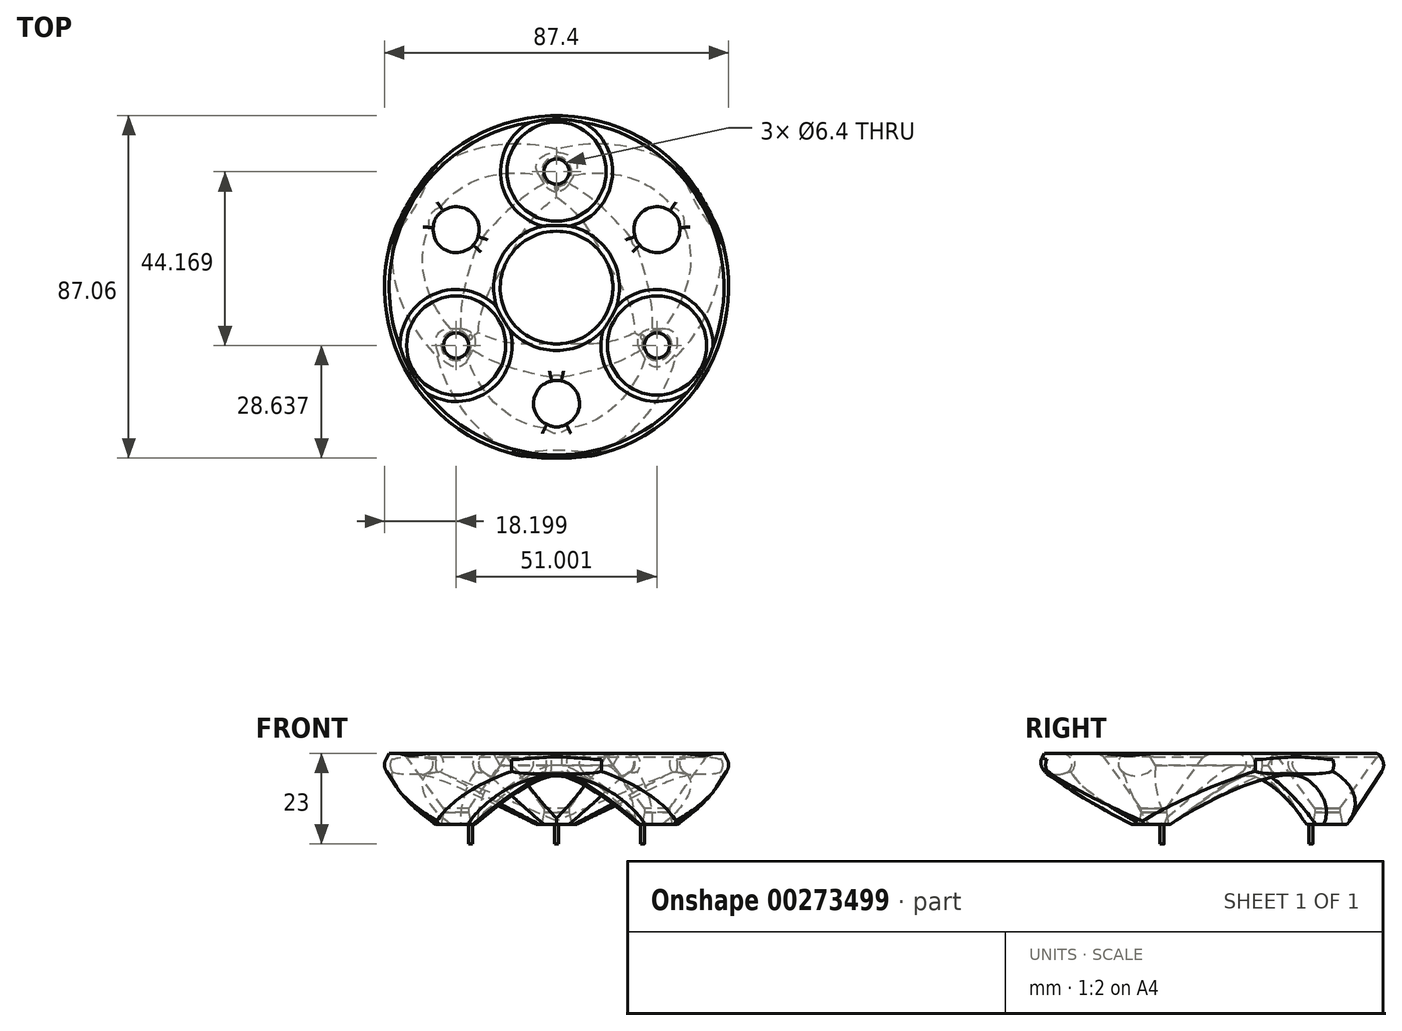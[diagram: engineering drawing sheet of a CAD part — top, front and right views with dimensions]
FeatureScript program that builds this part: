
annotation { "Feature Type Name" : "Feature", "Feature Type Description" : "" }
export const myFeature = defineFeature(function(context is Context, id is Id, definition is map)
    precondition{}
    {
        {
            var Q0;
            Q0=qCreatedBy(makeId("Top.planeOp"),FACE);
            var sketch = newSketch(context, id + "F0", { "sketchPlane" : qUnion([Q0])});
            skCircle(sketch, "E0", {"center": v(0, 0) * mm, "radius": 47.5 * mm});
            skCircle(sketch, "E1", {"center": v(0, 0) * mm, "radius": 11 * mm});
            skCircle(sketch, "E2", {"center": v(0, 29.45) * mm, "radius": 3.2 * mm});
            skCircle(sketch, "E3.1.0", {"center": v(-25.5, 14.72) * mm, "radius": 3.2 * mm});
            skCircle(sketch, "E3.2.0", {"center": v(-25.5, -14.72) * mm, "radius": 3.2 * mm});
            skCircle(sketch, "E4.1.3.0", {"center": v(0, -29.45) * mm, "radius": 3.2 * mm});
            skCircle(sketch, "E4.1.4.0", {"center": v(25.5, -14.72) * mm, "radius": 3.2 * mm});
            skCircle(sketch, "E4.1.5.0", {"center": v(25.5, 14.72) * mm, "radius": 3.2 * mm});
            skCircle(sketch, "E5", {"center": v(0, 25.2) * mm, "radius": 0.5 * mm});
            skCircle(sketch, "E6.1.0", {"center": v(-21.83, -12.6) * mm, "radius": 0.5 * mm});
            skCircle(sketch, "E6.2.0", {"center": v(21.83, -12.6) * mm, "radius": 0.5 * mm});
            skSolve(sketch);
        }
        {
            var Q0;
            Q0=makeQuery(id+"F0.imprint","IMPRINT",FACE,{"disambiguationData":[TD([[makeQuery(id+"F0.imprint","IMPRINT",EDGE,{"derivedFrom":sQuery(id+"F0.wireOp",EDGE,"E0")}),1.0]])]});
            var Q1;
            Q1=makeQuery(id+"F0.imprint","IMPRINT",FACE,{"disambiguationData":[TD([[makeQuery(id+"F0.imprint","IMPRINT",EDGE,{"derivedFrom":sQuery(id+"F0.wireOp",EDGE,"E6.1.0")}),1.0]])]});
            var Q2;
            Q2=makeQuery(id+"F0.imprint","IMPRINT",FACE,{"disambiguationData":[TD([[makeQuery(id+"F0.imprint","IMPRINT",EDGE,{"derivedFrom":sQuery(id+"F0.wireOp",EDGE,"E6.2.0")}),1.0]])]});
            var Q3;
            Q3=makeQuery(id+"F0.imprint","IMPRINT",FACE,{"disambiguationData":[TD([[makeQuery(id+"F0.imprint","IMPRINT",EDGE,{"derivedFrom":sQuery(id+"F0.wireOp",EDGE,"E5")}),1.0]])]});
            extrude(context, id + "F1", {"entities" : qUnion([Q0, Q1, Q2, Q3]), "depth" : 18 * mm, "offsetDistance" : 25 * mm});
        }
        {
            var Q0;
            Q0=makeQuery(id+"F0.imprint","IMPRINT",FACE,{"disambiguationData":[TD([[makeQuery(id+"F0.imprint","IMPRINT",EDGE,{"derivedFrom":sQuery(id+"F0.wireOp",EDGE,"E5")}),1.0]])]});
            var Q1;
            Q1=makeQuery(id+"F0.imprint","IMPRINT",FACE,{"disambiguationData":[TD([[makeQuery(id+"F0.imprint","IMPRINT",EDGE,{"derivedFrom":sQuery(id+"F0.wireOp",EDGE,"E6.1.0")}),1.0]])]});
            var Q2;
            Q2=makeQuery(id+"F0.imprint","IMPRINT",FACE,{"disambiguationData":[TD([[makeQuery(id+"F0.imprint","IMPRINT",EDGE,{"derivedFrom":sQuery(id+"F0.wireOp",EDGE,"E6.2.0")}),1.0]])]});
            extrude(context, id + "F2", {"entities" : qUnion([Q0, Q1, Q2]), "operationType" : NewBodyOperationType.ADD, "depth" : 10 * mm, "symmetric" : true});
        }
        {
            var Q0;
            Q0=makeQuery(id+"F1.opExtrude","CAP_EDGE",EDGE,{"disambiguationData":[OSD([sQuery(id+"F0.wireOp",EDGE,"E2")])],"isStart":false});
            var Q1;
            Q1=makeQuery(id+"F1.opExtrude","CAP_EDGE",EDGE,{"disambiguationData":[OSD([sQuery(id+"F0.wireOp",EDGE,"E4.1.4.0")])],"isStart":false});
            var Q2;
            Q2=makeQuery(id+"F1.opExtrude","CAP_EDGE",EDGE,{"disambiguationData":[OSD([sQuery(id+"F0.wireOp",EDGE,"E3.2.0")])],"isStart":false});
            chamfer(context, id + "F3", {"entities" : qUnion([Q0, Q1, Q2]), "chamferType" : ChamferType.TWO_OFFSETS, "width1" : 14 * mm, "oppositeDirection" : false, "width2" : 10 * mm, "tangentPropagation" : true});
        }
        {
            var Q0;
            Q0=makeQuery(id+"F1.opExtrude","CAP_EDGE",EDGE,{"disambiguationData":[OSD([sQuery(id+"F0.wireOp",EDGE,"E0")])],"isStart":true});
            chamfer(context, id + "F4", {"entities" : qUnion([Q0]), "chamferType" : ChamferType.TWO_OFFSETS, "width1" : 20 * mm, "oppositeDirection" : false, "width2" : 13 * mm, "tangentPropagation" : true});
        }
        {
            var Q0;
            Q0=makeQuery(id+"F1.opExtrude","CAP_EDGE",EDGE,{"disambiguationData":[OSD([sQuery(id+"F0.wireOp",EDGE,"E2")])],"isStart":true});
            var Q1;
            Q1=makeQuery(id+"F1.opExtrude","CAP_EDGE",EDGE,{"disambiguationData":[OSD([sQuery(id+"F0.wireOp",EDGE,"E3.2.0")])],"isStart":true});
            var Q2;
            Q2=makeQuery(id+"F1.opExtrude","CAP_EDGE",EDGE,{"disambiguationData":[OSD([sQuery(id+"F0.wireOp",EDGE,"E4.1.4.0")])],"isStart":true});
            chamfer(context, id + "F5", {"entities" : qUnion([Q0, Q1, Q2]), "chamferType" : ChamferType.TWO_OFFSETS, "width1" : 0.6 * mm, "oppositeDirection" : false, "width2" : 3 * mm, "tangentPropagation" : true});
        }
        {
            var Q0;
            Q0=makeQuery(id+"F1.opExtrude","CAP_EDGE",EDGE,{"disambiguationData":[OSD([sQuery(id+"F0.wireOp",EDGE,"E1")])],"isStart":true});
            chamfer(context, id + "F6", {"entities" : qUnion([Q0]), "chamferType" : ChamferType.TWO_OFFSETS, "width1" : 13 * mm, "oppositeDirection" : false, "width2" : 20 * mm, "tangentPropagation" : true});
        }
        {
            var Q0;
            Q0=makeQuery(id+"F1.opExtrude","CAP_EDGE",EDGE,{"disambiguationData":[OSD([sQuery(id+"F0.wireOp",EDGE,"E4.1.5.0")])],"isStart":true});
            var Q1;
            Q1=makeQuery(id+"F1.opExtrude","CAP_EDGE",EDGE,{"disambiguationData":[OSD([sQuery(id+"F0.wireOp",EDGE,"E4.1.3.0")])],"isStart":true});
            var Q2;
            Q2=makeQuery(id+"F1.opExtrude","CAP_EDGE",EDGE,{"disambiguationData":[OSD([sQuery(id+"F0.wireOp",EDGE,"E3.1.0")])],"isStart":true});
            chamfer(context, id + "F7", {"entities" : qUnion([Q0, Q1, Q2]), "chamferType" : ChamferType.TWO_OFFSETS, "width1" : 22 * mm, "oppositeDirection" : false, "width2" : 16 * mm, "tangentPropagation" : true});
        }
        {
            var Q0;
            {var subQ0=sQuery(id+"F0.wireOp",EDGE,"E0");Q0=makeQuery(id+"F4.opChamfer","BLEND_EDGE",EDGE,{"blendedFrom":[makeQuery(id+"F1.opExtrude","CAP_EDGE",EDGE,{"disambiguationData":[OSD([subQ0])],"isStart":true}),makeQuery(id+"F1.opExtrude","CAP_FACE",FACE,{"disambiguationData":[OSD([subQ0,sQuery(id+"F0.wireOp",EDGE,"E1"),sQuery(id+"F0.wireOp",EDGE,"E2"),sQuery(id+"F0.wireOp",EDGE,"E3.1.0"),sQuery(id+"F0.wireOp",EDGE,"E3.2.0")])],"isStart":false})],"blendedInto":[makeQuery(id+"F1.opExtrude","CAP_FACE",FACE,{"disambiguationData":[OSD([subQ0,sQuery(id+"F0.wireOp",EDGE,"E1"),sQuery(id+"F0.wireOp",EDGE,"E2"),sQuery(id+"F0.wireOp",EDGE,"E3.1.0"),sQuery(id+"F0.wireOp",EDGE,"E3.2.0")])],"isStart":false})]});}
            var Q1;
            {var subQ0=sQuery(id+"F0.wireOp",EDGE,"E1");Q1=makeQuery(id+"F6.opChamfer","BLEND_EDGE",EDGE,{"blendedFrom":[makeQuery(id+"F1.opExtrude","CAP_EDGE",EDGE,{"disambiguationData":[OSD([subQ0])],"isStart":true}),makeQuery(id+"F1.opExtrude","CAP_FACE",FACE,{"disambiguationData":[OSD([sQuery(id+"F0.wireOp",EDGE,"E0"),subQ0,sQuery(id+"F0.wireOp",EDGE,"E2"),sQuery(id+"F0.wireOp",EDGE,"E3.1.0"),sQuery(id+"F0.wireOp",EDGE,"E3.2.0")])],"isStart":false})],"blendedInto":[makeQuery(id+"F1.opExtrude","CAP_FACE",FACE,{"disambiguationData":[OSD([sQuery(id+"F0.wireOp",EDGE,"E0"),subQ0,sQuery(id+"F0.wireOp",EDGE,"E2"),sQuery(id+"F0.wireOp",EDGE,"E3.1.0"),sQuery(id+"F0.wireOp",EDGE,"E3.2.0")])],"isStart":false})]});}
            var Q2;
            {var subQ0=sQuery(id+"F0.wireOp",EDGE,"E3.2.0");Q2=makeQuery(id+"F3.opChamfer","BLEND_EDGE",EDGE,{"blendedFrom":[makeQuery(id+"F1.opExtrude","CAP_EDGE",EDGE,{"disambiguationData":[OSD([subQ0])],"isStart":false}),makeQuery(id+"F1.opExtrude","CAP_FACE",FACE,{"disambiguationData":[OSD([sQuery(id+"F0.wireOp",EDGE,"E0"),sQuery(id+"F0.wireOp",EDGE,"E1"),sQuery(id+"F0.wireOp",EDGE,"E2"),sQuery(id+"F0.wireOp",EDGE,"E3.1.0"),subQ0,sQuery(id+"F0.wireOp",EDGE,"E4.1.3.0"),sQuery(id+"F0.wireOp",EDGE,"E4.1.4.0"),sQuery(id+"F0.wireOp",EDGE,"E4.1.5.0")])],"isStart":false})],"blendedInto":[makeQuery(id+"F1.opExtrude","CAP_FACE",FACE,{"disambiguationData":[OSD([sQuery(id+"F0.wireOp",EDGE,"E0"),sQuery(id+"F0.wireOp",EDGE,"E1"),sQuery(id+"F0.wireOp",EDGE,"E2"),sQuery(id+"F0.wireOp",EDGE,"E3.1.0"),subQ0,sQuery(id+"F0.wireOp",EDGE,"E4.1.3.0"),sQuery(id+"F0.wireOp",EDGE,"E4.1.4.0"),sQuery(id+"F0.wireOp",EDGE,"E4.1.5.0")])],"isStart":false})]});}
            var Q3;
            {var subQ0=sQuery(id+"F0.wireOp",EDGE,"E2");Q3=makeQuery(id+"F3.opChamfer","BLEND_EDGE",EDGE,{"blendedFrom":[makeQuery(id+"F1.opExtrude","CAP_EDGE",EDGE,{"disambiguationData":[OSD([subQ0])],"isStart":false}),makeQuery(id+"F1.opExtrude","CAP_FACE",FACE,{"disambiguationData":[OSD([sQuery(id+"F0.wireOp",EDGE,"E0"),sQuery(id+"F0.wireOp",EDGE,"E1"),subQ0,sQuery(id+"F0.wireOp",EDGE,"E3.1.0"),sQuery(id+"F0.wireOp",EDGE,"E3.2.0"),sQuery(id+"F0.wireOp",EDGE,"E4.1.3.0"),sQuery(id+"F0.wireOp",EDGE,"E4.1.4.0"),sQuery(id+"F0.wireOp",EDGE,"E4.1.5.0")])],"isStart":false})],"blendedInto":[makeQuery(id+"F1.opExtrude","CAP_FACE",FACE,{"disambiguationData":[OSD([sQuery(id+"F0.wireOp",EDGE,"E0"),sQuery(id+"F0.wireOp",EDGE,"E1"),subQ0,sQuery(id+"F0.wireOp",EDGE,"E3.1.0"),sQuery(id+"F0.wireOp",EDGE,"E3.2.0"),sQuery(id+"F0.wireOp",EDGE,"E4.1.3.0"),sQuery(id+"F0.wireOp",EDGE,"E4.1.4.0"),sQuery(id+"F0.wireOp",EDGE,"E4.1.5.0")])],"isStart":false})]});}
            var Q4;
            {var subQ0=sQuery(id+"F0.wireOp",EDGE,"E4.1.4.0");Q4=makeQuery(id+"F3.opChamfer","BLEND_EDGE",EDGE,{"blendedFrom":[makeQuery(id+"F1.opExtrude","CAP_EDGE",EDGE,{"disambiguationData":[OSD([subQ0])],"isStart":false}),makeQuery(id+"F1.opExtrude","CAP_FACE",FACE,{"disambiguationData":[OSD([sQuery(id+"F0.wireOp",EDGE,"E0"),sQuery(id+"F0.wireOp",EDGE,"E1"),sQuery(id+"F0.wireOp",EDGE,"E2"),sQuery(id+"F0.wireOp",EDGE,"E3.1.0"),sQuery(id+"F0.wireOp",EDGE,"E3.2.0"),sQuery(id+"F0.wireOp",EDGE,"E4.1.3.0"),subQ0,sQuery(id+"F0.wireOp",EDGE,"E4.1.5.0")])],"isStart":false})],"blendedInto":[makeQuery(id+"F1.opExtrude","CAP_FACE",FACE,{"disambiguationData":[OSD([sQuery(id+"F0.wireOp",EDGE,"E0"),sQuery(id+"F0.wireOp",EDGE,"E1"),sQuery(id+"F0.wireOp",EDGE,"E2"),sQuery(id+"F0.wireOp",EDGE,"E3.1.0"),sQuery(id+"F0.wireOp",EDGE,"E3.2.0"),sQuery(id+"F0.wireOp",EDGE,"E4.1.3.0"),subQ0,sQuery(id+"F0.wireOp",EDGE,"E4.1.5.0")])],"isStart":false})]});}
            var Q5;
            {var subQ0=sQuery(id+"F0.wireOp",EDGE,"E3.1.0");Q5=makeQuery(id+"F7.opChamfer","BLEND_EDGE",EDGE,{"blendedFrom":[makeQuery(id+"F1.opExtrude","CAP_EDGE",EDGE,{"disambiguationData":[OSD([subQ0])],"isStart":true}),makeQuery(id+"F1.opExtrude","CAP_FACE",FACE,{"disambiguationData":[OSD([sQuery(id+"F0.wireOp",EDGE,"E0"),sQuery(id+"F0.wireOp",EDGE,"E1"),sQuery(id+"F0.wireOp",EDGE,"E2"),subQ0,sQuery(id+"F0.wireOp",EDGE,"E3.2.0"),sQuery(id+"F0.wireOp",EDGE,"E4.1.3.0"),sQuery(id+"F0.wireOp",EDGE,"E4.1.4.0"),sQuery(id+"F0.wireOp",EDGE,"E4.1.5.0")])],"isStart":false})],"blendedInto":[makeQuery(id+"F1.opExtrude","CAP_FACE",FACE,{"disambiguationData":[OSD([sQuery(id+"F0.wireOp",EDGE,"E0"),sQuery(id+"F0.wireOp",EDGE,"E1"),sQuery(id+"F0.wireOp",EDGE,"E2"),subQ0,sQuery(id+"F0.wireOp",EDGE,"E3.2.0"),sQuery(id+"F0.wireOp",EDGE,"E4.1.3.0"),sQuery(id+"F0.wireOp",EDGE,"E4.1.4.0"),sQuery(id+"F0.wireOp",EDGE,"E4.1.5.0")])],"isStart":false})]});}
            var Q6;
            {var subQ0=sQuery(id+"F0.wireOp",EDGE,"E4.1.3.0");Q6=makeQuery(id+"F7.opChamfer","BLEND_EDGE",EDGE,{"blendedFrom":[makeQuery(id+"F1.opExtrude","CAP_EDGE",EDGE,{"disambiguationData":[OSD([subQ0])],"isStart":true}),makeQuery(id+"F1.opExtrude","CAP_FACE",FACE,{"disambiguationData":[OSD([sQuery(id+"F0.wireOp",EDGE,"E0"),sQuery(id+"F0.wireOp",EDGE,"E1"),sQuery(id+"F0.wireOp",EDGE,"E2"),sQuery(id+"F0.wireOp",EDGE,"E3.1.0"),sQuery(id+"F0.wireOp",EDGE,"E3.2.0"),subQ0,sQuery(id+"F0.wireOp",EDGE,"E4.1.4.0"),sQuery(id+"F0.wireOp",EDGE,"E4.1.5.0")])],"isStart":false})],"blendedInto":[makeQuery(id+"F1.opExtrude","CAP_FACE",FACE,{"disambiguationData":[OSD([sQuery(id+"F0.wireOp",EDGE,"E0"),sQuery(id+"F0.wireOp",EDGE,"E1"),sQuery(id+"F0.wireOp",EDGE,"E2"),sQuery(id+"F0.wireOp",EDGE,"E3.1.0"),sQuery(id+"F0.wireOp",EDGE,"E3.2.0"),subQ0,sQuery(id+"F0.wireOp",EDGE,"E4.1.4.0"),sQuery(id+"F0.wireOp",EDGE,"E4.1.5.0")])],"isStart":false})]});}
            var Q7;
            {var subQ0=sQuery(id+"F0.wireOp",EDGE,"E4.1.5.0");Q7=makeQuery(id+"F7.opChamfer","BLEND_EDGE",EDGE,{"blendedFrom":[makeQuery(id+"F1.opExtrude","CAP_EDGE",EDGE,{"disambiguationData":[OSD([subQ0])],"isStart":true}),makeQuery(id+"F1.opExtrude","CAP_FACE",FACE,{"disambiguationData":[OSD([sQuery(id+"F0.wireOp",EDGE,"E0"),sQuery(id+"F0.wireOp",EDGE,"E1"),sQuery(id+"F0.wireOp",EDGE,"E2"),sQuery(id+"F0.wireOp",EDGE,"E3.1.0"),sQuery(id+"F0.wireOp",EDGE,"E3.2.0"),sQuery(id+"F0.wireOp",EDGE,"E4.1.3.0"),sQuery(id+"F0.wireOp",EDGE,"E4.1.4.0"),subQ0])],"isStart":false})],"blendedInto":[makeQuery(id+"F1.opExtrude","CAP_FACE",FACE,{"disambiguationData":[OSD([sQuery(id+"F0.wireOp",EDGE,"E0"),sQuery(id+"F0.wireOp",EDGE,"E1"),sQuery(id+"F0.wireOp",EDGE,"E2"),sQuery(id+"F0.wireOp",EDGE,"E3.1.0"),sQuery(id+"F0.wireOp",EDGE,"E3.2.0"),sQuery(id+"F0.wireOp",EDGE,"E4.1.3.0"),sQuery(id+"F0.wireOp",EDGE,"E4.1.4.0"),subQ0])],"isStart":false})]});}
            chamfer(context, id + "F8", {"entities" : qUnion([Q0, Q1, Q2, Q3, Q4, Q5, Q6, Q7]), "width" : 2 * mm, "tangentPropagation" : true});
        }
        {
            var Q0;
            Q0=makeQuery(id+"F7.opChamfer","BLEND_EDGE",EDGE,{"blendedFrom":[makeQuery(id+"F1.opExtrude","CAP_EDGE",EDGE,{"disambiguationData":[OSD([sQuery(id+"F0.wireOp",EDGE,"E4.1.5.0")])],"isStart":true}),makeQuery(id+"F6.opChamfer","BLEND_FACE",FACE,{"disambiguationData":[OSD([sQuery(id+"F0.wireOp",EDGE,"E1")])]})],"blendedInto":[makeQuery(id+"F6.opChamfer","BLEND_FACE",FACE,{"disambiguationData":[OSD([sQuery(id+"F0.wireOp",EDGE,"E1")])]})]});
            var Q1;
            Q1=makeQuery(id+"F7.opChamfer","BLEND_EDGE",EDGE,{"blendedFrom":[makeQuery(id+"F1.opExtrude","CAP_EDGE",EDGE,{"disambiguationData":[OSD([sQuery(id+"F0.wireOp",EDGE,"E3.1.0")])],"isStart":true}),makeQuery(id+"F6.opChamfer","BLEND_FACE",FACE,{"disambiguationData":[OSD([sQuery(id+"F0.wireOp",EDGE,"E1")])]})],"blendedInto":[makeQuery(id+"F6.opChamfer","BLEND_FACE",FACE,{"disambiguationData":[OSD([sQuery(id+"F0.wireOp",EDGE,"E1")])]})]});
            var Q2;
            Q2=makeQuery(id+"F7.opChamfer","BLEND_EDGE",EDGE,{"blendedFrom":[makeQuery(id+"F1.opExtrude","CAP_EDGE",EDGE,{"disambiguationData":[OSD([sQuery(id+"F0.wireOp",EDGE,"E4.1.3.0")])],"isStart":true}),makeQuery(id+"F6.opChamfer","BLEND_FACE",FACE,{"disambiguationData":[OSD([sQuery(id+"F0.wireOp",EDGE,"E1")])]})],"blendedInto":[makeQuery(id+"F6.opChamfer","BLEND_FACE",FACE,{"disambiguationData":[OSD([sQuery(id+"F0.wireOp",EDGE,"E1")])]})]});
            var Q3;
            Q3=makeQuery(id+"F7.opChamfer","BLEND_EDGE",EDGE,{"blendedFrom":[makeQuery(id+"F1.opExtrude","CAP_EDGE",EDGE,{"disambiguationData":[OSD([sQuery(id+"F0.wireOp",EDGE,"E3.1.0")])],"isStart":true}),makeQuery(id+"F4.opChamfer","BLEND_FACE",FACE,{"disambiguationData":[OSD([sQuery(id+"F0.wireOp",EDGE,"E0")])]})],"blendedInto":[makeQuery(id+"F4.opChamfer","BLEND_FACE",FACE,{"disambiguationData":[OSD([sQuery(id+"F0.wireOp",EDGE,"E0")])]})]});
            var Q4;
            Q4=makeQuery(id+"F7.opChamfer","BLEND_EDGE",EDGE,{"blendedFrom":[makeQuery(id+"F1.opExtrude","CAP_EDGE",EDGE,{"disambiguationData":[OSD([sQuery(id+"F0.wireOp",EDGE,"E4.1.5.0")])],"isStart":true}),makeQuery(id+"F4.opChamfer","BLEND_FACE",FACE,{"disambiguationData":[OSD([sQuery(id+"F0.wireOp",EDGE,"E0")])]})],"blendedInto":[makeQuery(id+"F4.opChamfer","BLEND_FACE",FACE,{"disambiguationData":[OSD([sQuery(id+"F0.wireOp",EDGE,"E0")])]})]});
            var Q5;
            Q5=makeQuery(id+"F7.opChamfer","BLEND_EDGE",EDGE,{"blendedFrom":[makeQuery(id+"F1.opExtrude","CAP_EDGE",EDGE,{"disambiguationData":[OSD([sQuery(id+"F0.wireOp",EDGE,"E4.1.3.0")])],"isStart":true}),makeQuery(id+"F4.opChamfer","BLEND_FACE",FACE,{"disambiguationData":[OSD([sQuery(id+"F0.wireOp",EDGE,"E0")])]})],"blendedInto":[makeQuery(id+"F4.opChamfer","BLEND_FACE",FACE,{"disambiguationData":[OSD([sQuery(id+"F0.wireOp",EDGE,"E0")])]})]});
            var Q6;
            {var subQ0=sQuery(id+"F0.wireOp",EDGE,"E3.1.0");Q6=makeQuery(id+"F7.opChamfer","BLEND_EDGE",EDGE,{"blendedFrom":[makeQuery(id+"F1.opExtrude","CAP_EDGE",EDGE,{"disambiguationData":[OSD([subQ0])],"isStart":true}),makeQuery(id+"F1.opExtrude","SWEPT_FACE",FACE,{"disambiguationData":[OSD([subQ0])]})],"blendedInto":[makeQuery(id+"F1.opExtrude","SWEPT_FACE",FACE,{"disambiguationData":[OSD([subQ0])]})]});}
            var Q7;
            {var subQ0=sQuery(id+"F0.wireOp",EDGE,"E4.1.5.0");Q7=makeQuery(id+"F7.opChamfer","BLEND_EDGE",EDGE,{"blendedFrom":[makeQuery(id+"F1.opExtrude","CAP_EDGE",EDGE,{"disambiguationData":[OSD([subQ0])],"isStart":true}),makeQuery(id+"F1.opExtrude","SWEPT_FACE",FACE,{"disambiguationData":[OSD([subQ0])]})],"blendedInto":[makeQuery(id+"F1.opExtrude","SWEPT_FACE",FACE,{"disambiguationData":[OSD([subQ0])]})]});}
            var Q8;
            {var subQ0=sQuery(id+"F0.wireOp",EDGE,"E4.1.3.0");Q8=makeQuery(id+"F7.opChamfer","BLEND_EDGE",EDGE,{"blendedFrom":[makeQuery(id+"F1.opExtrude","CAP_EDGE",EDGE,{"disambiguationData":[OSD([subQ0])],"isStart":true}),makeQuery(id+"F1.opExtrude","SWEPT_FACE",FACE,{"disambiguationData":[OSD([subQ0])]})],"blendedInto":[makeQuery(id+"F1.opExtrude","SWEPT_FACE",FACE,{"disambiguationData":[OSD([subQ0])]})]});}
            fillet(context, id + "F9", {"entities" : qUnion([Q0, Q1, Q2, Q3, Q4, Q5, Q6, Q7, Q8]), "radius" : 6 * mm, "tangentPropagation" : true, "allowEdgeOverflow" : false});
        }
        {
            var Q0;
            {var subQ0=sQuery(id+"F0.wireOp",EDGE,"E4.1.5.0");Q0=makeQuery(id+"F3XoC3uYJy4NfSD_1.opFillet","BLEND_EDGE",EDGE,{"blendedFrom":[makeQuery(id+"F1.opExtrude","CAP_EDGE",EDGE,{"disambiguationData":[OSD([subQ0])],"isStart":false}),makeQuery(id+"F9.opFillet","BLEND_FACE",FACE,{"disambiguationData":[OSD([subQ0])]})],"blendedInto":[makeQuery(id+"F9.opFillet","BLEND_FACE",FACE,{"disambiguationData":[OSD([subQ0])]})]});}
            var Q1;
            {var subQ0=sQuery(id+"F0.wireOp",EDGE,"E3.1.0");Q1=makeQuery(id+"F3XoC3uYJy4NfSD_1.opFillet","BLEND_EDGE",EDGE,{"blendedFrom":[makeQuery(id+"F1.opExtrude","CAP_EDGE",EDGE,{"disambiguationData":[OSD([subQ0])],"isStart":false}),makeQuery(id+"F9.opFillet","BLEND_FACE",FACE,{"disambiguationData":[OSD([subQ0])]})],"blendedInto":[makeQuery(id+"F9.opFillet","BLEND_FACE",FACE,{"disambiguationData":[OSD([subQ0])]})]});}
            var Q2;
            {var subQ0=sQuery(id+"F0.wireOp",EDGE,"E4.1.3.0");Q2=makeQuery(id+"F3XoC3uYJy4NfSD_1.opFillet","BLEND_EDGE",EDGE,{"blendedFrom":[makeQuery(id+"F1.opExtrude","CAP_EDGE",EDGE,{"disambiguationData":[OSD([subQ0])],"isStart":false}),makeQuery(id+"F9.opFillet","BLEND_FACE",FACE,{"disambiguationData":[OSD([subQ0])]})],"blendedInto":[makeQuery(id+"F9.opFillet","BLEND_FACE",FACE,{"disambiguationData":[OSD([subQ0])]})]});}
            var Q3;
            {var subQ0=sQuery(id+"F0.wireOp",EDGE,"E0");Q3=makeQuery(id+"F8.opChamfer","BLEND_EDGE",EDGE,{"blendedFrom":[makeQuery(id+"F4.opChamfer","BLEND_EDGE",EDGE,{"blendedFrom":[makeQuery(id+"F1.opExtrude","CAP_EDGE",EDGE,{"disambiguationData":[OSD([subQ0])],"isStart":true}),makeQuery(id+"F1.opExtrude","CAP_FACE",FACE,{"disambiguationData":[OSD([subQ0,sQuery(id+"F0.wireOp",EDGE,"E1"),sQuery(id+"F0.wireOp",EDGE,"E2"),sQuery(id+"F0.wireOp",EDGE,"E3.1.0"),sQuery(id+"F0.wireOp",EDGE,"E3.2.0"),sQuery(id+"F0.wireOp",EDGE,"E4.1.3.0"),sQuery(id+"F0.wireOp",EDGE,"E4.1.4.0"),sQuery(id+"F0.wireOp",EDGE,"E4.1.5.0")])],"isStart":false})],"blendedInto":[makeQuery(id+"F1.opExtrude","CAP_FACE",FACE,{"disambiguationData":[OSD([subQ0,sQuery(id+"F0.wireOp",EDGE,"E1"),sQuery(id+"F0.wireOp",EDGE,"E2"),sQuery(id+"F0.wireOp",EDGE,"E3.1.0"),sQuery(id+"F0.wireOp",EDGE,"E3.2.0"),sQuery(id+"F0.wireOp",EDGE,"E4.1.3.0"),sQuery(id+"F0.wireOp",EDGE,"E4.1.4.0"),sQuery(id+"F0.wireOp",EDGE,"E4.1.5.0")])],"isStart":false})]}),makeQuery(id+"F4.opChamfer","BLEND_FACE",FACE,{"disambiguationData":[OSD([subQ0])]})],"blendedInto":[makeQuery(id+"F4.opChamfer","BLEND_FACE",FACE,{"disambiguationData":[OSD([subQ0])]})]});}
            fillet(context, id + "F10", {"entities" : qUnion([Q0, Q1, Q2, Q3]), "radius" : 3 * mm, "tangentPropagation" : true, "allowEdgeOverflow" : false});
        }
        {
            var Q0;
            {var subQ0=sQuery(id+"F0.wireOp",EDGE,"E3.1.0");Q0=makeQuery(id+"F9.opFillet","BLEND_EDGE",EDGE,{"blendedFrom":[makeQuery(id+"F7.opChamfer","BLEND_EDGE",EDGE,{"blendedFrom":[makeQuery(id+"F1.opExtrude","CAP_EDGE",EDGE,{"disambiguationData":[OSD([subQ0])],"isStart":true}),makeQuery(id+"F1.opExtrude","SWEPT_FACE",FACE,{"disambiguationData":[OSD([subQ0])]})],"blendedInto":[makeQuery(id+"F1.opExtrude","SWEPT_FACE",FACE,{"disambiguationData":[OSD([subQ0])]})]}),makeQuery(id+"F1.opExtrude","CAP_FACE",FACE,{"disambiguationData":[OSD([sQuery(id+"F0.wireOp",EDGE,"E0"),sQuery(id+"F0.wireOp",EDGE,"E1"),sQuery(id+"F0.wireOp",EDGE,"E2"),subQ0,sQuery(id+"F0.wireOp",EDGE,"E3.2.0"),sQuery(id+"F0.wireOp",EDGE,"E4.1.3.0"),sQuery(id+"F0.wireOp",EDGE,"E4.1.4.0"),sQuery(id+"F0.wireOp",EDGE,"E4.1.5.0")])],"isStart":false})],"blendedInto":[makeQuery(id+"F1.opExtrude","CAP_FACE",FACE,{"disambiguationData":[OSD([sQuery(id+"F0.wireOp",EDGE,"E0"),sQuery(id+"F0.wireOp",EDGE,"E1"),sQuery(id+"F0.wireOp",EDGE,"E2"),subQ0,sQuery(id+"F0.wireOp",EDGE,"E3.2.0"),sQuery(id+"F0.wireOp",EDGE,"E4.1.3.0"),sQuery(id+"F0.wireOp",EDGE,"E4.1.4.0"),sQuery(id+"F0.wireOp",EDGE,"E4.1.5.0")])],"isStart":false})]});}
            var Q1;
            {var subQ0=sQuery(id+"F0.wireOp",EDGE,"E4.1.5.0");Q1=makeQuery(id+"F9.opFillet","BLEND_EDGE",EDGE,{"blendedFrom":[makeQuery(id+"F7.opChamfer","BLEND_EDGE",EDGE,{"blendedFrom":[makeQuery(id+"F1.opExtrude","CAP_EDGE",EDGE,{"disambiguationData":[OSD([subQ0])],"isStart":true}),makeQuery(id+"F1.opExtrude","SWEPT_FACE",FACE,{"disambiguationData":[OSD([subQ0])]})],"blendedInto":[makeQuery(id+"F1.opExtrude","SWEPT_FACE",FACE,{"disambiguationData":[OSD([subQ0])]})]}),makeQuery(id+"F1.opExtrude","CAP_FACE",FACE,{"disambiguationData":[OSD([sQuery(id+"F0.wireOp",EDGE,"E0"),sQuery(id+"F0.wireOp",EDGE,"E1"),sQuery(id+"F0.wireOp",EDGE,"E2"),sQuery(id+"F0.wireOp",EDGE,"E3.1.0"),sQuery(id+"F0.wireOp",EDGE,"E3.2.0"),sQuery(id+"F0.wireOp",EDGE,"E4.1.3.0"),sQuery(id+"F0.wireOp",EDGE,"E4.1.4.0"),subQ0])],"isStart":false})],"blendedInto":[makeQuery(id+"F1.opExtrude","CAP_FACE",FACE,{"disambiguationData":[OSD([sQuery(id+"F0.wireOp",EDGE,"E0"),sQuery(id+"F0.wireOp",EDGE,"E1"),sQuery(id+"F0.wireOp",EDGE,"E2"),sQuery(id+"F0.wireOp",EDGE,"E3.1.0"),sQuery(id+"F0.wireOp",EDGE,"E3.2.0"),sQuery(id+"F0.wireOp",EDGE,"E4.1.3.0"),sQuery(id+"F0.wireOp",EDGE,"E4.1.4.0"),subQ0])],"isStart":false})]});}
            var Q2;
            {var subQ0=sQuery(id+"F0.wireOp",EDGE,"E4.1.3.0");Q2=makeQuery(id+"F9.opFillet","BLEND_EDGE",EDGE,{"blendedFrom":[makeQuery(id+"F7.opChamfer","BLEND_EDGE",EDGE,{"blendedFrom":[makeQuery(id+"F1.opExtrude","CAP_EDGE",EDGE,{"disambiguationData":[OSD([subQ0])],"isStart":true}),makeQuery(id+"F1.opExtrude","SWEPT_FACE",FACE,{"disambiguationData":[OSD([subQ0])]})],"blendedInto":[makeQuery(id+"F1.opExtrude","SWEPT_FACE",FACE,{"disambiguationData":[OSD([subQ0])]})]}),makeQuery(id+"F1.opExtrude","CAP_FACE",FACE,{"disambiguationData":[OSD([sQuery(id+"F0.wireOp",EDGE,"E0"),sQuery(id+"F0.wireOp",EDGE,"E1"),sQuery(id+"F0.wireOp",EDGE,"E2"),sQuery(id+"F0.wireOp",EDGE,"E3.1.0"),sQuery(id+"F0.wireOp",EDGE,"E3.2.0"),subQ0,sQuery(id+"F0.wireOp",EDGE,"E4.1.4.0"),sQuery(id+"F0.wireOp",EDGE,"E4.1.5.0")])],"isStart":false})],"blendedInto":[makeQuery(id+"F1.opExtrude","CAP_FACE",FACE,{"disambiguationData":[OSD([sQuery(id+"F0.wireOp",EDGE,"E0"),sQuery(id+"F0.wireOp",EDGE,"E1"),sQuery(id+"F0.wireOp",EDGE,"E2"),sQuery(id+"F0.wireOp",EDGE,"E3.1.0"),sQuery(id+"F0.wireOp",EDGE,"E3.2.0"),subQ0,sQuery(id+"F0.wireOp",EDGE,"E4.1.4.0"),sQuery(id+"F0.wireOp",EDGE,"E4.1.5.0")])],"isStart":false})]});}
            fillet(context, id + "F11", {"entities" : qUnion([Q0, Q1, Q2]), "radius" : 2.6 * mm, "tangentPropagation" : true, "allowEdgeOverflow" : false});
        }
    });
